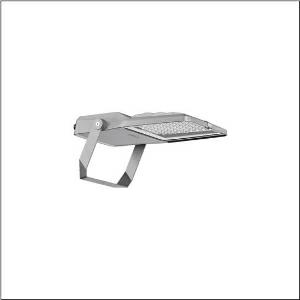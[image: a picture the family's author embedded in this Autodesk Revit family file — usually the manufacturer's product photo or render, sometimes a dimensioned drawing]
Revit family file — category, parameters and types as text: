
# Revit family: floodlight_fl_21_iq_mini___pl64_5xa7772c1e1a_659a
name_source: partatom
category: Lighting Fixtures
units: mm (PartAtom-declared; Revit-internal decimal feet)

## family parameters
Cut with Voids When Loaded = No
Host = Face
Light Source = No
Part Type = Normal
Room Calculation Point = No
Round Connector Dimension = Use Diameter
Shared = No

## types (1)
- --- (1 x LED, 9770 lm, 87.2 W, 2200K)
    Apparent Load = 87 VA
    CIE Flux Codes = 28 80 98 100 100
    Color Rendering = 70
    Color Temperature = 2200K
    Default Elevation = 1800 mm
    Description = Floodlight FL 21 iQ mini, floodlight, primary light control with lens, of PMMA, primary optical cover: protective disc, of toughened safety glass, transparent, light distribution: PL64, light emission: direct distribution, installation type: surface-mounted, lamps: LED, High Power LED, rated values: 9.770lm | 87,2W | 112lm/W (begin service life); end service life: 9.770lm | 92,1W; at 50% lumin. flux: 4.885lm | 40,1W | 121,8lm/W, colour temperature: 2200K, colour rendering: CRI > 70, light colour: 722, light setting 1 begin service life: 100% | 9.770lm | 87,2W | 112lm/W | 2.200K, light setting 1 end service life: 92,1W, further light settings possible, control: Street-Remote, Auto-Match, Temp-Guard, Night-Set, Smart-Wire, Desk-Remote (wireless, voltage-free reading and setting of iQ features in the workshop via application-optimized NFC function/RFID function), optimised constant luminous flux control (CLO 2.0), pre-setting: linear dimming characteristic, with terminal, 6-pole, mains connection: 220..240V, AC, 50/60Hz, luminaire housing, of diecast aluminium, powder-coated, SITECO metallic grey (DB 702S), corrosivity category C5 mid according to DIN EN ISO 12944suitable for swimming poolschlorine-resistant, sealing non-destructively replaceable, mounting bracket, of steel, galvanised, powder-coated, SITECO metallic grey (DB 702S), protection rating (complete): IP66, insulation class (complete): insulation class II (safety insulation), certification: CE, ENEC, VDE, protection symbol: D, impact resistance: IK08, permissible operating ambient temperature: -40..+40°C, permissible operating ambient temperature for outdoor applications: -40..+50°C, standard: DIN EN 12944, LABS conformity tested according to VDMA 24364:2018-05, packaging unit: 1 piece

Light Distribution: PL64
    Height = 70 mm
    Lamp = 1 x LED
    Lamp Light Flux = 9770 lm
    Lamp Power = 87.2 W
    Lamp count = 1
    Length = 485 mm
    Luminous efficacy = 112 lm/W
    Manufacturer = Siteco
    ModVariant = No
    Model = 5XA7772C1E1A
    Number of Poles = 1
    OnlyDefault = Yes
    Power Factor = 1
    Product Name = Floodlight FL 21 iQ mini | PL64
    Product group = floodlight | pylon annexe
    ProductGroupID = 6201
    Protection Class = Protection class II
    Protection Degree = IP 66
    RLX_Detail_Level = 1
    RLX_Emergency_Light_Flux = 0 lm
    RLX_Emergency_Type = 0
    RLX_Emergency_Type_DB = No
    RlxData = <blob elided: 96545 chars, md5=11edfb58>
    Socket = socket
    Standby Power = 0 W
    System Light Flux = 9770 lm
    System Power = 87 W
    Type Comments = factory setting: luminous flux: 100 % | dim-lin: 254 | 456 mA
    Type Image = l_1006845.jpg
    URL = http://relux.com
    VarID = @adj_165947
    Voltage = 0 V
    Weight = 0.00 kg
    Width = 337 mm

## geometry (parser evidence)
native form markers: Blend x4, Sweep x12
no freeform markers — native parametric forms only
